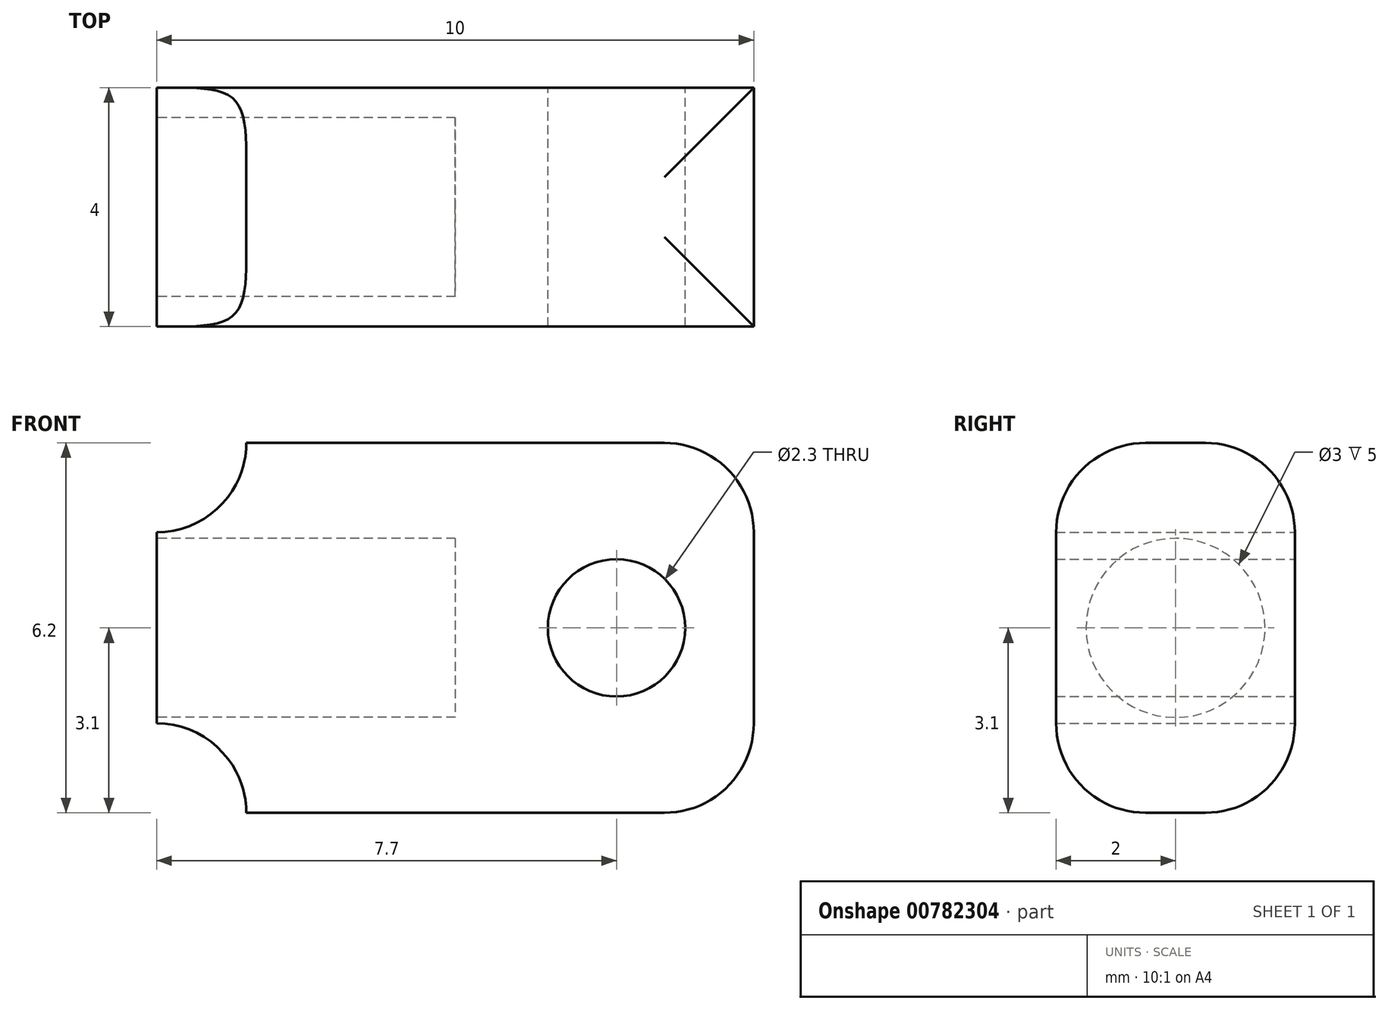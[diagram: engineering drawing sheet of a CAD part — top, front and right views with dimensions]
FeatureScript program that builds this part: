
annotation { "Feature Type Name" : "Feature", "Feature Type Description" : "" }
export const myFeature = defineFeature(function(context is Context, id is Id, definition is map)
    precondition{}
    {
        {
            var Q0;
            Q0=qCreatedBy(makeId("Front.planeOp"),FACE);
            var sketch = newSketch(context, id + "F0", { "sketchPlane" : qUnion([Q0])});
            skLineSegment(sketch, "E0.bottom", {"start": v(-3.5, -3.1) * mm, "end": v(5, -3.1) * mm});
            skLineSegment(sketch, "E0.top", {"start": v(-3.5, 3.1) * mm, "end": v(5, 3.1) * mm});
            skLineSegment(sketch, "E0.left", {"start": v(-5, -1.6) * mm, "end": v(-5, 1.6) * mm});
            skLineSegment(sketch, "E0.right", {"start": v(5, -3.1) * mm, "end": v(5, 3.1) * mm});
            skPoint(sketch, "E0.middle", {"position": v(0, 0) * mm});
            skArc(sketch, "E1", {"start": v(-5, 1.6) * mm, "mid": v(-3.94, 2.04) * mm, "end": v(-3.5, 3.1) * mm});
            skArc(sketch, "E2.MirrorCS", {"start": v(-5, -1.6) * mm, "mid": v(-3.94, -2.04) * mm, "end": v(-3.5, -3.1) * mm});
            skCircle(sketch, "E3", {"center": v(2.7, 0) * mm, "radius": 1.15 * mm});
            skSolve(sketch);
        }
        {
            var Q0;
            Q0 = qSketchRegion(id + "F0", true);
            extrude(context, id + "F1", {"entities" : qUnion([Q0]), "depth" : 4 * mm, "offsetDistance" : 25 * mm});
        }
        {
            var Q0;
            Q0=makeQuery(id+"F1.opExtrude","SWEPT_FACE",FACE,{"disambiguationData":[OSD([sQuery(id+"F0.wireOp",EDGE,"E0.left")])]});
            var sketch = newSketch(context, id + "F2", { "sketchPlane" : qUnion([Q0])});
            skCircle(sketch, "E4", {"center": v(2, 0) * mm, "radius": 1.5 * mm});
            skPoint(sketch, "E4.centerSnap0", {"position": v(2, 1.6) * mm});
            skSolve(sketch);
        }
        {
            var Q0;
            Q0 = qSketchRegion(id + "F2", true);
            extrude(context, id + "F3", {"entities" : qUnion([Q0]), "operationType" : NewBodyOperationType.REMOVE, "oppositeDirection" : true, "depth" : 5 * mm, "offsetDistance" : 25 * mm});
        }
        {
            var Q0;
            Q0=makeQuery(id+"F1.opExtrude","CAP_EDGE",EDGE,{"disambiguationData":[OSD([sQuery(id+"F0.wireOp",EDGE,"E0.bottom")])],"isStart":false});
            var Q1;
            Q1=makeQuery(id+"F1.opExtrude","CAP_EDGE",EDGE,{"disambiguationData":[OSD([sQuery(id+"F0.wireOp",EDGE,"E0.top")])],"isStart":false});
            var Q2;
            Q2=makeQuery(id+"F1.opExtrude","CAP_EDGE",EDGE,{"disambiguationData":[OSD([sQuery(id+"F0.wireOp",EDGE,"E0.bottom")])],"isStart":true});
            var Q3;
            Q3=makeQuery(id+"F1.opExtrude","CAP_EDGE",EDGE,{"disambiguationData":[OSD([sQuery(id+"F0.wireOp",EDGE,"E0.top")])],"isStart":true});
            var Q4;
            Q4=makeQuery(id+"F1.opExtrude","SWEPT_EDGE",EDGE,{"disambiguationData":[OSD([sQuery(id+"F0.wireOp",EDGE,"E0.top"),sQuery(id+"F0.wireOp",EDGE,"E0.right")])]});
            var Q5;
            Q5=makeQuery(id+"F1.opExtrude","SWEPT_EDGE",EDGE,{"disambiguationData":[OSD([sQuery(id+"F0.wireOp",EDGE,"E0.bottom"),sQuery(id+"F0.wireOp",EDGE,"E0.right")])]});
            fillet(context, id + "F4", {"entities" : qUnion([Q0, Q1, Q2, Q3, Q4, Q5]), "radius" : 1.5 * mm, "tangentPropagation" : true, "allowEdgeOverflow" : false});
        }
    });
